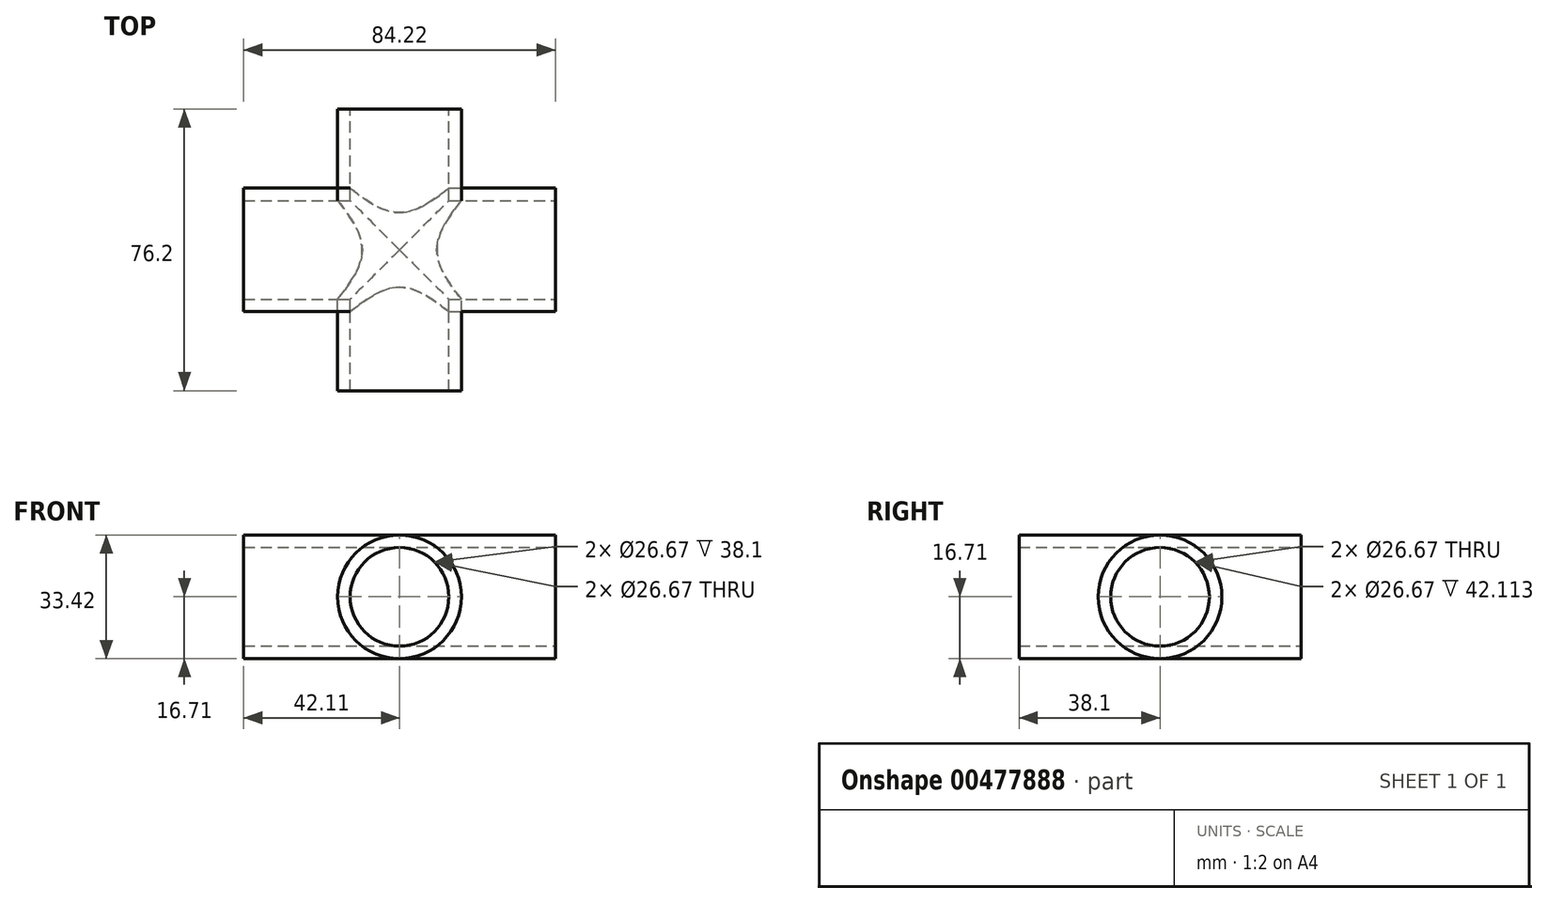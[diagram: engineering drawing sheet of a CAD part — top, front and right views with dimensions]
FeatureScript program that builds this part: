
annotation { "Feature Type Name" : "Feature", "Feature Type Description" : "" }
export const myFeature = defineFeature(function(context is Context, id is Id, definition is map)
    precondition{}
    {
        {
            var Q0;
            Q0=qCreatedBy(makeId("Top.planeOp"),FACE);
            var sketch = newSketch(context, id + "F0", { "sketchPlane" : qUnion([Q0])});
            skLineSegment(sketch, "E0", {"start": v(0, 38.1) * mm, "end": v(0, 0) * mm});
            skLineSegment(sketch, "E1", {"start": v(0, 0) * mm, "end": v(0, -38.1) * mm});
            skLineSegment(sketch, "E2", {"start": v(0, 0) * mm, "end": v(42.11, 0) * mm});
            skLineSegment(sketch, "E3", {"start": v(42.11, 0) * mm, "end": v(42.11, 16.71) * mm});
            skLineSegment(sketch, "E4", {"start": v(42.11, 16.71) * mm, "end": v(16.71, 16.71) * mm});
            skLineSegment(sketch, "E5", {"start": v(16.71, 16.71) * mm, "end": v(16.71, 38.1) * mm});
            skLineSegment(sketch, "E6", {"start": v(16.71, 38.1) * mm, "end": v(-16.71, 38.1) * mm});
            skLineSegment(sketch, "E7", {"start": v(-16.71, 38.1) * mm, "end": v(-16.71, 16.71) * mm});
            skLineSegment(sketch, "E8", {"start": v(-16.71, -38.1) * mm, "end": v(16.71, -38.1) * mm});
            skLineSegment(sketch, "E9", {"start": v(16.71, -38.1) * mm, "end": v(16.71, -16.71) * mm});
            skLineSegment(sketch, "E10", {"start": v(16.71, -16.71) * mm, "end": v(42.11, -16.71) * mm});
            skLineSegment(sketch, "E11", {"start": v(42.11, -16.71) * mm, "end": v(42.11, 0) * mm});
            skLineSegment(sketch, "E12", {"start": v(16.71, 16.71) * mm, "end": v(0, 16.71) * mm});
            skPoint(sketch, "E12.endSnap0", {"position": v(0, 19.05) * mm});
            skLineSegment(sketch, "E13", {"start": v(16.71, -16.71) * mm, "end": v(0, -16.71) * mm});
            skLineSegment(sketch, "E14", {"start": v(0, 16.71) * mm, "end": v(-16.71, 16.71) * mm});
            skLineSegment(sketch, "E15", {"start": v(42.11, 13.33) * mm, "end": v(3.29, 13.33) * mm});
            skLineSegment(sketch, "E16", {"start": v(42.11, -13.34) * mm, "end": v(3.29, -13.34) * mm});
            skLineSegment(sketch, "E17", {"start": v(-13.33, -38.1) * mm, "end": v(-13.33, -16.71) * mm});
            skLineSegment(sketch, "E18", {"start": v(3.29, 13.33) * mm, "end": v(0, 13.33) * mm});
            skLineSegment(sketch, "E19", {"start": v(3.29, -13.34) * mm, "end": v(0, -13.34) * mm});
            skLineSegment(sketch, "E20", {"start": v(13.34, 16.71) * mm, "end": v(13.34, 38.1) * mm});
            skLineSegment(sketch, "E21", {"start": v(13.34, -16.71) * mm, "end": v(13.34, -38.1) * mm});
            skLineSegment(sketch, "E22", {"start": v(13.34, -27.4) * mm, "end": v(16.71, -27.4) * mm, "construction": true});
            skLineSegment(sketch, "E23", {"start": v(16.71, 27.4) * mm, "end": v(13.33, 27.4) * mm, "construction": true});
            skLineSegment(sketch, "E24", {"start": v(-13.33, 27.4) * mm, "end": v(-16.71, 27.4) * mm, "construction": true});
            skLineSegment(sketch, "E25", {"start": v(29.41, 16.71) * mm, "end": v(29.41, 13.33) * mm, "construction": true});
            skLineSegment(sketch, "E26", {"start": v(29.41, -16.71) * mm, "end": v(29.41, -13.33) * mm, "construction": true});
            skLineSegment(sketch, "E27", {"start": v(-16.71, 16.71) * mm, "end": v(-42.11, 16.71) * mm});
            skLineSegment(sketch, "E28", {"start": v(-42.11, 16.71) * mm, "end": v(-42.11, -16.71) * mm});
            skLineSegment(sketch, "E29", {"start": v(-42.11, -16.71) * mm, "end": v(-16.71, -16.71) * mm});
            skLineSegment(sketch, "E30", {"start": v(-16.71, -16.71) * mm, "end": v(-13.33, -16.71) * mm});
            skLineSegment(sketch, "E31", {"start": v(-13.33, -16.71) * mm, "end": v(0, -16.71) * mm});
            skLineSegment(sketch, "E32", {"start": v(0, 13.33) * mm, "end": v(-13.33, 13.33) * mm});
            skLineSegment(sketch, "E33", {"start": v(-13.33, 13.33) * mm, "end": v(-16.71, 13.33) * mm});
            skLineSegment(sketch, "E34", {"start": v(0, -13.34) * mm, "end": v(-13.33, -13.34) * mm});
            skLineSegment(sketch, "E35", {"start": v(-13.33, -13.34) * mm, "end": v(-16.71, -13.34) * mm});
            skLineSegment(sketch, "E36.trimOffspring", {"start": v(-13.33, 16.71) * mm, "end": v(-13.33, 38.1) * mm});
            skLineSegment(sketch, "E37", {"start": v(-16.71, 13.33) * mm, "end": v(-42.11, 13.33) * mm});
            skLineSegment(sketch, "E38", {"start": v(-16.71, -13.34) * mm, "end": v(-42.11, -13.34) * mm});
            skLineSegment(sketch, "E39.trimOffspring", {"start": v(-16.71, -16.71) * mm, "end": v(-16.71, -38.1) * mm});
            skLineSegment(sketch, "E40", {"start": v(-13.33, -27.4) * mm, "end": v(-16.71, -27.4) * mm, "construction": true});
            skLineSegment(sketch, "E41", {"start": v(0, 0) * mm, "end": v(-42.11, 0) * mm});
            skLineSegment(sketch, "E42", {"start": v(-16.71, 16.71) * mm, "end": v(-16.71, -16.71) * mm});
            skLineSegment(sketch, "E43", {"start": v(16.71, 16.71) * mm, "end": v(16.71, -16.71) * mm});
            skLineSegment(sketch, "E44", {"start": v(-13.33, 16.71) * mm, "end": v(-13.33, -16.71) * mm});
            skLineSegment(sketch, "E45", {"start": v(13.34, 16.71) * mm, "end": v(13.34, -16.71) * mm});
            skSolve(sketch);
        }
        {
            var Q0;
            {var subQ0=sQuery(id+"F0.wireOp",EDGE,"E27");Q0=makeQuery(id+"F0.imprint","IMPRINT",FACE,{"disambiguationData":[TD([[makeQuery(id+"F0.imprint","IMPRINT",EDGE,{"derivedFrom":subQ0}),1.0]])]});}
            var Q1;
            {var subQ5=sQuery(id+"F0.wireOp",EDGE,"E33");Q1=makeQuery(id+"F0.imprint","IMPRINT",FACE,{"disambiguationData":[TD([[makeQuery(id+"F0.imprint","IMPRINT",EDGE,{"derivedFrom":subQ5}),-1.0]])]});}
            var Q2;
            {var subQ3=sQuery(id+"F0.wireOp",EDGE,"E32");Q2=makeQuery(id+"F0.imprint","IMPRINT",FACE,{"disambiguationData":[TD([[makeQuery(id+"F0.imprint","IMPRINT",EDGE,{"derivedFrom":subQ3}),-1.0]])]});}
            var Q3;
            {var subQ0=sQuery(id+"F0.wireOp",EDGE,"E18");Q3=makeQuery(id+"F0.imprint","IMPRINT",FACE,{"disambiguationData":[TD([[makeQuery(id+"F0.imprint","IMPRINT",EDGE,{"derivedFrom":subQ0}),-1.0]])]});}
            var Q4;
            {var subQ0=sQuery(id+"F0.wireOp",EDGE,"E43");var subQ5=sQuery(id+"F0.wireOp",EDGE,"E15");var subQ6=makeQuery(id+"F0.imprint","INTERSECT",VERTEX,{"derivedFrom":[subQ5,subQ0]});Q4=makeQuery(id+"F0.imprint","IMPRINT",FACE,{"disambiguationData":[TD([[makeQuery(id+"F0.imprint","IMPRINT",EDGE,{"disambiguationData":[TD([[subQ6,-1.0]])],"derivedFrom":subQ5}),-1.0]])]});}
            var Q5;
            {var subQ0=sQuery(id+"F0.wireOp",EDGE,"E4");Q5=makeQuery(id+"F0.imprint","IMPRINT",FACE,{"disambiguationData":[TD([[makeQuery(id+"F0.imprint","IMPRINT",EDGE,{"derivedFrom":subQ0}),1.0]])]});}
            var Q6;
            Q6=sQuery(id+"F0.wireOp",EDGE,"E41");
            revolve(context, id + "F1", {"entities" : qUnion([Q0, Q1, Q2, Q3, Q4, Q5]), "axis" : qUnion([Q6]), "revolveType" : RevolveType.FULL});
        }
        {
            var Q0;
            {var subQ2=sQuery(id+"F0.wireOp",EDGE,"E17");Q0=makeQuery(id+"F0.imprint","IMPRINT",FACE,{"disambiguationData":[TD([[makeQuery(id+"F0.imprint","IMPRINT",EDGE,{"derivedFrom":subQ2}),1.0]])]});}
            var Q1;
            {var subQ0=sQuery(id+"F0.wireOp",EDGE,"E30");Q1=makeQuery(id+"F0.imprint","IMPRINT",FACE,{"disambiguationData":[TD([[makeQuery(id+"F0.imprint","IMPRINT",EDGE,{"derivedFrom":subQ0}),1.0]])]});}
            var Q2;
            {var subQ0=sQuery(id+"F0.wireOp",EDGE,"E35");Q2=makeQuery(id+"F0.imprint","IMPRINT",FACE,{"disambiguationData":[TD([[makeQuery(id+"F0.imprint","IMPRINT",EDGE,{"derivedFrom":subQ0}),-1.0]])]});}
            var Q3;
            {var subQ0=sQuery(id+"F0.wireOp",EDGE,"E33");Q3=makeQuery(id+"F0.imprint","IMPRINT",FACE,{"disambiguationData":[TD([[makeQuery(id+"F0.imprint","IMPRINT",EDGE,{"derivedFrom":subQ0}),1.0]])]});}
            var Q4;
            {var subQ5=sQuery(id+"F0.wireOp",EDGE,"E33");Q4=makeQuery(id+"F0.imprint","IMPRINT",FACE,{"disambiguationData":[TD([[makeQuery(id+"F0.imprint","IMPRINT",EDGE,{"derivedFrom":subQ5}),-1.0]])]});}
            var Q5;
            {var subQ0=sQuery(id+"F0.wireOp",EDGE,"E7");Q5=makeQuery(id+"F0.imprint","IMPRINT",FACE,{"disambiguationData":[TD([[makeQuery(id+"F0.imprint","IMPRINT",EDGE,{"derivedFrom":subQ0}),1.0]])]});}
            var Q6;
            Q6=sQuery(id+"F0.wireOp",EDGE,"E0");
            revolve(context, id + "F2", {"entities" : qUnion([Q0, Q1, Q2, Q3, Q4, Q5]), "axis" : qUnion([Q6]), "revolveType" : RevolveType.FULL});
        }
        {
            var Q0;
            Q0=makeQuery(id+"F1.opRevolve","SWEPT_FACE",FACE,{"disambiguationData":[OSD([sQuery(id+"F0.wireOp",EDGE,"E3")])]});
            var sketch = newSketch(context, id + "F3", { "sketchPlane" : qUnion([Q0])});
            skCircle(sketch, "E46.0", {"center": v(0, 0) * mm, "radius": 13.33 * mm});
            skSolve(sketch);
        }
        {
            var Q0;
            Q0=makeQuery(id+"F3.imprint","IMPRINT",FACE,{"disambiguationData":[TD([[makeQuery(id+"F3.imprint","IMPRINT",EDGE,{"derivedFrom":sQuery(id+"F3.wireOp",EDGE,"E46.0")}),1.0]])]});
            extrude(context, id + "F4", {"entities" : qUnion([Q0]), "operationType" : NewBodyOperationType.REMOVE, "endBound" : BoundingType.THROUGH_ALL, "oppositeDirection" : true, "depth" : 25.4 * mm, "offsetDistance" : 25.4 * mm});
        }
        {
            var Q0;
            Q0=makeQuery(id+"F2.opRevolve","SWEPT_FACE",FACE,{"disambiguationData":[OSD([sQuery(id+"F0.wireOp",EDGE,"E6")])]});
            var sketch = newSketch(context, id + "F5", { "sketchPlane" : qUnion([Q0])});
            skCircle(sketch, "E47.0", {"center": v(0, 0) * mm, "radius": 13.33 * mm});
            skSolve(sketch);
        }
        {
            var Q0;
            Q0=makeQuery(id+"F5.imprint","IMPRINT",FACE,{"disambiguationData":[TD([[makeQuery(id+"F5.imprint","IMPRINT",EDGE,{"derivedFrom":sQuery(id+"F5.wireOp",EDGE,"E47.0")}),1.0]])]});
            extrude(context, id + "F6", {"entities" : qUnion([Q0]), "operationType" : NewBodyOperationType.REMOVE, "endBound" : BoundingType.THROUGH_ALL, "oppositeDirection" : true, "depth" : 25.4 * mm, "offsetDistance" : 25.4 * mm});
        }
    });
